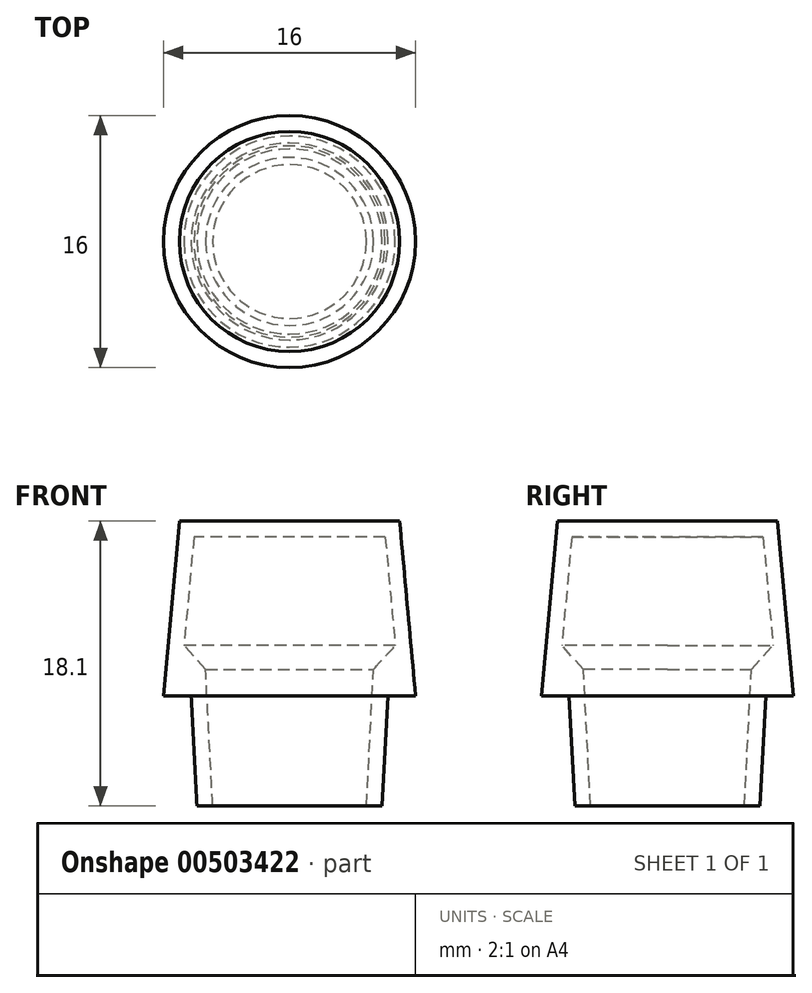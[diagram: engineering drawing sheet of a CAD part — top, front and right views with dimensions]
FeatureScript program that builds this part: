
annotation { "Feature Type Name" : "Feature", "Feature Type Description" : "" }
export const myFeature = defineFeature(function(context is Context, id is Id, definition is map)
    precondition{}
    {
        {
            var Q0;
            Q0=qCreatedBy(makeId("Top.planeOp"),FACE);
            var sketch = newSketch(context, id + "F0", { "sketchPlane" : qUnion([Q0])});
            skCircle(sketch, "E0", {"center": v(0, 0) * mm, "radius": 8 * mm});
            skSolve(sketch);
        }
        {
            var Q0;
            Q0=makeQuery(id+"F0.imprint","IMPRINT",FACE,{"disambiguationData":[TD([[makeQuery(id+"F0.imprint","IMPRINT",EDGE,{"derivedFrom":sQuery(id+"F0.wireOp",EDGE,"E0")}),1.0]])]});
            extrude(context, id + "F1", {"entities" : qUnion([Q0]), "depth" : 11.1 * mm, "hasDraft" : true, "draftAngle" : 5.2 * degree, "draftPullDirection" : true});
        }
        {
            var Q0;
            Q0=makeQuery(id+"F1.opExtrude","CAP_FACE",FACE,{"disambiguationData":[OSD([sQuery(id+"F0.wireOp",EDGE,"E0")])],"isStart":true});
            var sketch = newSketch(context, id + "F2", { "sketchPlane" : qUnion([Q0])});
            skCircle(sketch, "E1", {"center": v(0, 0) * mm, "radius": 6.25 * mm});
            skSolve(sketch);
        }
        {
            var Q0;
            Q0=makeQuery(id+"F2.imprint","IMPRINT",FACE,{"disambiguationData":[TD([[makeQuery(id+"F2.imprint","IMPRINT",EDGE,{"derivedFrom":sQuery(id+"F2.wireOp",EDGE,"E1")}),1.0]])]});
            extrude(context, id + "F3", {"entities" : qUnion([Q0]), "operationType" : NewBodyOperationType.ADD, "depth" : 7 * mm, "hasDraft" : true, "draftAngle" : 3 * degree, "draftPullDirection" : true});
        }
        {
            var Q0;
            Q0=makeQuery(id+"F3.opExtrude","CAP_FACE",FACE,{"disambiguationData":[OSD([sQuery(id+"F2.wireOp",EDGE,"E1")])],"isStart":false});
            shell(context, id + "F4", {"entities" : qUnion([Q0]), "thickness" : 1 * mm});
        }
        {
            var Q0;
            {var subQ0=sQuery(id+"F0.wireOp",EDGE,"E0");Q0=makeQuery(id+"F4.opShell","OFFSET_EDGE",EDGE,{"disambiguationData":[OSD([subQ0]),TDD([makeQuery(id+"F1.opExtrude","CAP_EDGE",EDGE,{"disambiguationData":[OSD([subQ0])],"isStart":true})])]});}
            chamfer(context, id + "F5", {"entities" : qUnion([Q0]), "width" : 2 * mm, "tangentPropagation" : true});
        }
    });
